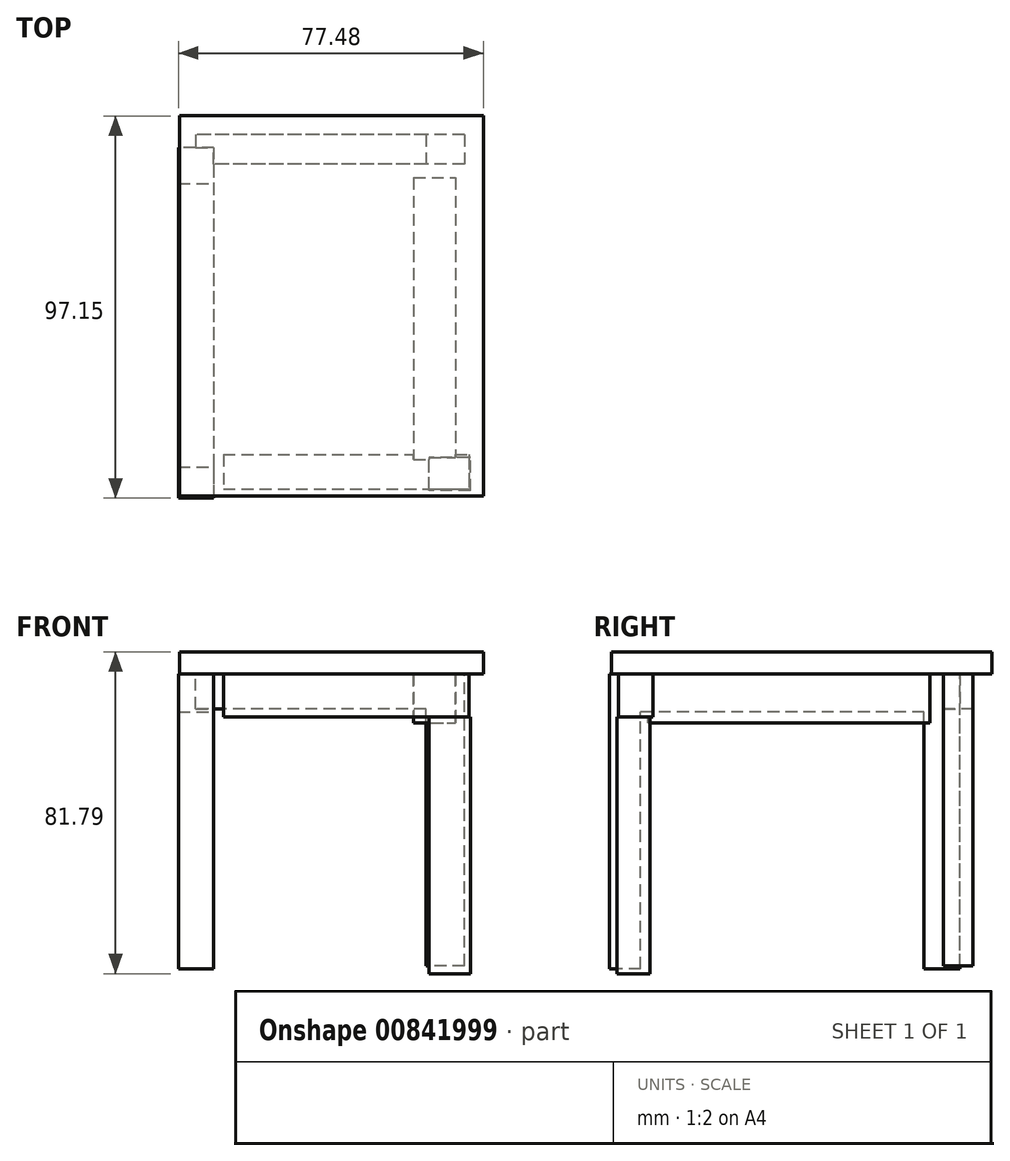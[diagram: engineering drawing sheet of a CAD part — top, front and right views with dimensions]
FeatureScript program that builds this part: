
annotation { "Feature Type Name" : "Feature", "Feature Type Description" : "" }
export const myFeature = defineFeature(function(context is Context, id is Id, definition is map)
    precondition{}
    {
        {
            var Q0;
            Q0=qCreatedBy(makeId("Top.planeOp"),FACE);
            var sketch = newSketch(context, id + "F0", { "sketchPlane" : qUnion([Q0])});
            skLineSegment(sketch, "E0.bottom", {"start": v(-77.17, -61.67) * mm, "end": v(0, -61.67) * mm});
            skLineSegment(sketch, "E0.top", {"start": v(-77.17, 34.94) * mm, "end": v(0, 34.94) * mm});
            skLineSegment(sketch, "E0.left", {"start": v(-77.17, -61.67) * mm, "end": v(-77.17, 34.94) * mm});
            skLineSegment(sketch, "E0.right", {"start": v(0, -61.67) * mm, "end": v(0, 34.94) * mm});
            skSolve(sketch);
        }
        {
            var Q0;
            Q0=makeQuery(id+"F0.imprint","IMPRINT",FACE,{"disambiguationData":[TD([[makeQuery(id+"F0.imprint","IMPRINT",EDGE,{"derivedFrom":sQuery(id+"F0.wireOp",EDGE,"E0.bottom")}),1.0]])]});
            extrude(context, id + "F1", {"entities" : qUnion([Q0]), "depth" : 5.6 * mm, "offsetDistance" : 25.4 * mm});
        }
        {
            var Q0;
            Q0=makeQuery(id+"F1.opExtrude","CAP_FACE",FACE,{"disambiguationData":[OSD([sQuery(id+"F0.wireOp",EDGE,"E0.bottom"),sQuery(id+"F0.wireOp",EDGE,"E0.top"),sQuery(id+"F0.wireOp",EDGE,"E0.left"),sQuery(id+"F0.wireOp",EDGE,"E0.right")])],"isStart":true});
            var sketch = newSketch(context, id + "F2", { "sketchPlane" : qUnion([Q0])});
            skLineSegment(sketch, "E1.bottom", {"start": v(-4.8, -30.18) * mm, "end": v(-73.1, -30.18) * mm});
            skLineSegment(sketch, "E1.top", {"start": v(-4.8, -22.64) * mm, "end": v(-73.1, -22.64) * mm});
            skLineSegment(sketch, "E1.left", {"start": v(-4.8, -30.18) * mm, "end": v(-4.8, -22.64) * mm});
            skLineSegment(sketch, "E1.right", {"start": v(-73.1, -30.18) * mm, "end": v(-73.1, -22.64) * mm});
            skSolve(sketch);
        }
        {
            var Q0;
            Q0 = qSketchRegion(id + "F2", true);
            extrude(context, id + "F3", {"entities" : qUnion([Q0]), "operationType" : NewBodyOperationType.ADD, "depth" : 8.9 * mm, "offsetDistance" : 25.4 * mm});
        }
        {
            var Q0;
            Q0=makeQuery(id+"F1.opExtrude","CAP_FACE",FACE,{"disambiguationData":[OSD([sQuery(id+"F0.wireOp",EDGE,"E0.bottom"),sQuery(id+"F0.wireOp",EDGE,"E0.top"),sQuery(id+"F0.wireOp",EDGE,"E0.left"),sQuery(id+"F0.wireOp",EDGE,"E0.right")])],"isStart":true});
            var sketch = newSketch(context, id + "F4", { "sketchPlane" : qUnion([Q0])});
            skSolve(sketch);
        }
        {
            var Q0;
            Q0=makeQuery(id+"F4.imprint","IMPRINT",FACE,{"disambiguationData":[TD([[makeQuery(id+"F4.imprint","IMPRINT",EDGE,{"derivedFrom":makeQuery(id+"F1.opExtrude","CAP_EDGE",EDGE,{"disambiguationData":[OSD([sQuery(id+"F0.wireOp",EDGE,"E0.bottom")])],"isStart":true})}),-1.0]])]});
            var sketch = newSketch(context, id + "F5", { "sketchPlane" : qUnion([Q0])});
            skLineSegment(sketch, "E2.bottom", {"start": v(-68.53, -26.9) * mm, "end": v(-77.48, -26.9) * mm});
            skLineSegment(sketch, "E2.top", {"start": v(-68.53, 62.21) * mm, "end": v(-77.48, 62.21) * mm});
            skLineSegment(sketch, "E2.left", {"start": v(-68.53, -26.9) * mm, "end": v(-68.53, 62.21) * mm});
            skLineSegment(sketch, "E2.right", {"start": v(-77.48, -26.9) * mm, "end": v(-77.48, 62.21) * mm});
            skSolve(sketch);
        }
        {
            var Q0;
            Q0 = qSketchRegion(id + "F5", true);
            extrude(context, id + "F6", {"entities" : qUnion([Q0]), "operationType" : NewBodyOperationType.ADD, "depth" : 9.65 * mm, "offsetDistance" : 25.4 * mm});
        }
        {
            var Q0;
            Q0=makeQuery(id+"F4.imprint","IMPRINT",FACE,{"disambiguationData":[TD([[makeQuery(id+"F4.imprint","IMPRINT",EDGE,{"derivedFrom":makeQuery(id+"F1.opExtrude","CAP_EDGE",EDGE,{"disambiguationData":[OSD([sQuery(id+"F0.wireOp",EDGE,"E0.bottom")])],"isStart":true})}),-1.0]])]});
            var sketch = newSketch(context, id + "F7", { "sketchPlane" : qUnion([Q0])});
            skLineSegment(sketch, "E3.bottom", {"start": v(-66.04, 51.14) * mm, "end": v(-3.67, 51.14) * mm});
            skLineSegment(sketch, "E3.top", {"start": v(-66.04, 59.86) * mm, "end": v(-3.67, 59.86) * mm});
            skLineSegment(sketch, "E3.left", {"start": v(-66.04, 51.14) * mm, "end": v(-66.04, 59.86) * mm});
            skLineSegment(sketch, "E3.right", {"start": v(-3.67, 51.14) * mm, "end": v(-3.67, 59.86) * mm});
            skSolve(sketch);
        }
        {
            var Q0;
            Q0 = qSketchRegion(id + "F7", true);
            extrude(context, id + "F8", {"entities" : qUnion([Q0]), "operationType" : NewBodyOperationType.ADD, "depth" : 10.92 * mm, "offsetDistance" : 25.4 * mm});
        }
        {
            var Q0;
            Q0=makeQuery(id+"F4.imprint","IMPRINT",FACE,{"disambiguationData":[TD([[makeQuery(id+"F4.imprint","IMPRINT",EDGE,{"derivedFrom":makeQuery(id+"F1.opExtrude","CAP_EDGE",EDGE,{"disambiguationData":[OSD([sQuery(id+"F0.wireOp",EDGE,"E0.bottom")])],"isStart":true})}),-1.0]])]});
            var sketch = newSketch(context, id + "F9", { "sketchPlane" : qUnion([Q0])});
            skLineSegment(sketch, "E4.bottom", {"start": v(-17.7, -19.2) * mm, "end": v(-7.1, -19.2) * mm});
            skLineSegment(sketch, "E4.top", {"start": v(-17.7, 52.43) * mm, "end": v(-7.1, 52.43) * mm});
            skLineSegment(sketch, "E4.left", {"start": v(-17.7, -19.2) * mm, "end": v(-17.7, 52.43) * mm});
            skLineSegment(sketch, "E4.right", {"start": v(-7.1, -19.2) * mm, "end": v(-7.1, 52.43) * mm});
            skSolve(sketch);
        }
        {
            var Q0;
            Q0 = qSketchRegion(id + "F9", true);
            extrude(context, id + "F10", {"entities" : qUnion([Q0]), "operationType" : NewBodyOperationType.ADD, "depth" : 12.45 * mm, "offsetDistance" : 25.4 * mm});
        }
        {
            var Q0;
            Q0=makeQuery(id+"F6.opExtrude","CAP_FACE",FACE,{"disambiguationData":[OSD([sQuery(id+"F5.wireOp",EDGE,"E2.bottom"),sQuery(id+"F5.wireOp",EDGE,"E2.top"),sQuery(id+"F5.wireOp",EDGE,"E2.left"),sQuery(id+"F5.wireOp",EDGE,"E2.right")])],"isStart":false});
            var sketch = newSketch(context, id + "F11", { "sketchPlane" : qUnion([Q0])});
            skLineSegment(sketch, "E5.bottom", {"start": v(-77.48, 54.25) * mm, "end": v(-68.53, 54.25) * mm});
            skLineSegment(sketch, "E5.top", {"start": v(-77.48, 62.21) * mm, "end": v(-68.53, 62.21) * mm});
            skLineSegment(sketch, "E5.left", {"start": v(-77.48, 54.25) * mm, "end": v(-77.48, 62.21) * mm});
            skLineSegment(sketch, "E5.right", {"start": v(-68.53, 54.25) * mm, "end": v(-68.53, 62.21) * mm});
            skSolve(sketch);
        }
        {
            var Q0;
            Q0 = qSketchRegion(id + "F11", true);
            extrude(context, id + "F12", {"entities" : qUnion([Q0]), "operationType" : NewBodyOperationType.ADD, "depth" : 65.28 * mm, "offsetDistance" : 25.4 * mm});
        }
        {
            var Q0;
            Q0=makeQuery(id+"F6.opExtrude","CAP_FACE",FACE,{"disambiguationData":[OSD([sQuery(id+"F5.wireOp",EDGE,"E2.bottom"),sQuery(id+"F5.wireOp",EDGE,"E2.top"),sQuery(id+"F5.wireOp",EDGE,"E2.left"),sQuery(id+"F5.wireOp",EDGE,"E2.right")])],"isStart":false});
            var sketch = newSketch(context, id + "F13", { "sketchPlane" : qUnion([Q0])});
            skLineSegment(sketch, "E6.bottom", {"start": v(-77.48, -26.9) * mm, "end": v(-68.53, -26.9) * mm});
            skLineSegment(sketch, "E6.top", {"start": v(-77.48, -17.75) * mm, "end": v(-68.53, -17.75) * mm});
            skLineSegment(sketch, "E6.left", {"start": v(-77.48, -26.9) * mm, "end": v(-77.48, -17.75) * mm});
            skLineSegment(sketch, "E6.right", {"start": v(-68.53, -26.9) * mm, "end": v(-68.53, -17.75) * mm});
            skSolve(sketch);
        }
        {
            var Q0;
            Q0 = qSketchRegion(id + "F13", true);
            extrude(context, id + "F14", {"entities" : qUnion([Q0]), "operationType" : NewBodyOperationType.ADD, "depth" : 65.28 * mm, "offsetDistance" : 25.4 * mm});
        }
        {
            var Q0;
            Q0=makeQuery(id+"F8.opExtrude","CAP_FACE",FACE,{"disambiguationData":[OSD([sQuery(id+"F7.wireOp",EDGE,"E3.bottom"),sQuery(id+"F7.wireOp",EDGE,"E3.top"),sQuery(id+"F7.wireOp",EDGE,"E3.left"),sQuery(id+"F7.wireOp",EDGE,"E3.right")])],"isStart":false});
            var sketch = newSketch(context, id + "F15", { "sketchPlane" : qUnion([Q0])});
            skSolve(sketch);
        }
        {
            var Q0;
            {var subQ2=sQuery(id+"F7.wireOp",EDGE,"E3.top");Q0=makeQuery(id+"F15.imprint","IMPRINT",FACE,{"disambiguationData":[TD([[makeQuery(id+"F15.imprint","IMPRINT",EDGE,{"derivedFrom":makeQuery(id+"F8.opExtrude","CAP_EDGE",EDGE,{"disambiguationData":[OSD([subQ2])],"isStart":false})}),-1.0]])]});}
            var sketch = newSketch(context, id + "F16", { "sketchPlane" : qUnion([Q0])});
            skLineSegment(sketch, "E7.bottom", {"start": v(-3.34, 60.27) * mm, "end": v(-13.8, 60.27) * mm});
            skLineSegment(sketch, "E7.top", {"start": v(-3.34, 51.89) * mm, "end": v(-13.8, 51.89) * mm});
            skLineSegment(sketch, "E7.left", {"start": v(-3.34, 60.27) * mm, "end": v(-3.34, 51.89) * mm});
            skLineSegment(sketch, "E7.right", {"start": v(-13.8, 60.27) * mm, "end": v(-13.8, 51.89) * mm});
            skSolve(sketch);
        }
        {
            var Q0;
            Q0 = qSketchRegion(id + "F16", true);
            extrude(context, id + "F17", {"entities" : qUnion([Q0]), "operationType" : NewBodyOperationType.ADD, "depth" : 65.28 * mm, "offsetDistance" : 25.4 * mm});
        }
        {
            var Q0;
            Q0=makeQuery(id+"F3.opExtrude","CAP_FACE",FACE,{"disambiguationData":[OSD([sQuery(id+"F2.wireOp",EDGE,"E1.bottom"),sQuery(id+"F2.wireOp",EDGE,"E1.top"),sQuery(id+"F2.wireOp",EDGE,"E1.left"),sQuery(id+"F2.wireOp",EDGE,"E1.right")])],"isStart":false});
            var sketch = newSketch(context, id + "F18", { "sketchPlane" : qUnion([Q0])});
            skLineSegment(sketch, "E8.bottom", {"start": v(-4.8, -30.18) * mm, "end": v(-14.6, -30.18) * mm});
            skLineSegment(sketch, "E8.top", {"start": v(-4.8, -22.64) * mm, "end": v(-14.6, -22.64) * mm});
            skLineSegment(sketch, "E8.left", {"start": v(-4.8, -30.18) * mm, "end": v(-4.8, -22.64) * mm});
            skLineSegment(sketch, "E8.right", {"start": v(-14.6, -30.18) * mm, "end": v(-14.6, -22.64) * mm});
            skSolve(sketch);
        }
        {
            var Q0;
            Q0 = qSketchRegion(id + "F18", true);
            extrude(context, id + "F19", {"entities" : qUnion([Q0]), "operationType" : NewBodyOperationType.ADD, "depth" : 65.28 * mm, "offsetDistance" : 25.4 * mm});
        }
    });
